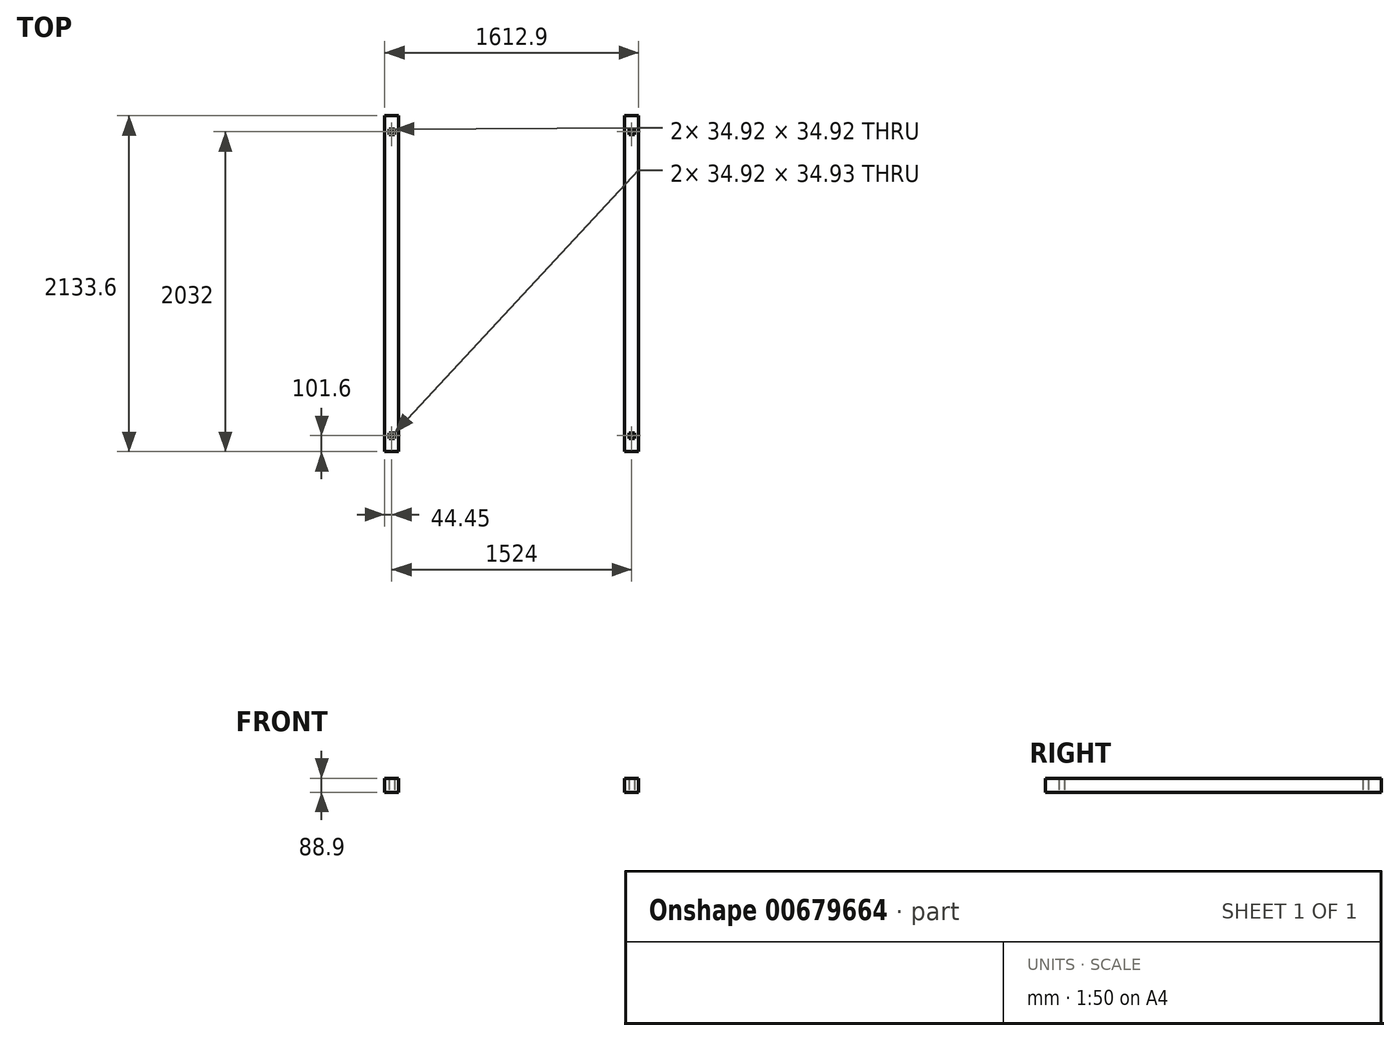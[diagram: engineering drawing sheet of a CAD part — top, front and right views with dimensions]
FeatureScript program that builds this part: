
annotation { "Feature Type Name" : "Feature", "Feature Type Description" : "" }
export const myFeature = defineFeature(function(context is Context, id is Id, definition is map)
    precondition{}
    {
        {
            var Q0;
            Q0=qCreatedBy(makeId("Front.planeOp"),FACE);
            var sketch = newSketch(context, id + "F0", { "sketchPlane" : qUnion([Q0])});
            skLineSegment(sketch, "E0.bottom", {"start": v(0, 0) * mm, "end": v(88.9, 0) * mm});
            skLineSegment(sketch, "E0.top", {"start": v(0, 88.9) * mm, "end": v(88.9, 88.9) * mm});
            skLineSegment(sketch, "E0.left", {"start": v(0, 0) * mm, "end": v(0, 88.9) * mm});
            skLineSegment(sketch, "E0.right", {"start": v(88.9, 0) * mm, "end": v(88.9, 88.9) * mm});
            skSolve(sketch);
        }
        {
            var Q0;
            Q0=makeQuery(id+"F0.imprint","IMPRINT",FACE,{"disambiguationData":[TD([[makeQuery(id+"F0.imprint","IMPRINT",EDGE,{"derivedFrom":sQuery(id+"F0.wireOp",EDGE,"E0.bottom")}),1.0]])]});
            extrude(context, id + "F1", {"entities" : qUnion([Q0]), "depth" : 2133.6 * mm, "offsetDistance" : 25.4 * mm});
        }
        {
            var Q0;
            Q0=makeQuery(id+"F1.opExtrude","SWEPT_FACE",FACE,{"disambiguationData":[OSD([sQuery(id+"F0.wireOp",EDGE,"E0.bottom")])]});
            var sketch = newSketch(context, id + "F2", { "sketchPlane" : qUnion([Q0])});
            skLineSegment(sketch, "E1.bottom", {"start": v(26.99, 119.06) * mm, "end": v(61.91, 119.06) * mm});
            skLineSegment(sketch, "E1.top", {"start": v(26.99, 84.14) * mm, "end": v(61.91, 84.14) * mm});
            skLineSegment(sketch, "E1.left", {"start": v(26.99, 119.06) * mm, "end": v(26.99, 84.14) * mm});
            skLineSegment(sketch, "E1.right", {"start": v(61.91, 119.06) * mm, "end": v(61.91, 84.14) * mm});
            skSolve(sketch);
        }
        {
            var Q0;
            Q0=makeQuery(id+"F2.imprint","IMPRINT",FACE,{"disambiguationData":[TD([[makeQuery(id+"F2.imprint","IMPRINT",EDGE,{"derivedFrom":sQuery(id+"F2.wireOp",EDGE,"E1.bottom")}),-1.0]])]});
            extrude(context, id + "F3", {"entities" : qUnion([Q0]), "operationType" : NewBodyOperationType.REMOVE, "oppositeDirection" : true, "depth" : 91.44 * mm, "offsetDistance" : 25.4 * mm});
        }
        {
            var Q0;
            Q0=makeQuery(id+"F1.opExtrude","SWEPT_FACE",FACE,{"disambiguationData":[OSD([sQuery(id+"F0.wireOp",EDGE,"E0.bottom")])]});
            var sketch = newSketch(context, id + "F4", { "sketchPlane" : qUnion([Q0])});
            skLineSegment(sketch, "E2.bottom", {"start": v(26.99, 2049.46) * mm, "end": v(61.91, 2049.46) * mm});
            skLineSegment(sketch, "E2.top", {"start": v(26.99, 2014.54) * mm, "end": v(61.91, 2014.54) * mm});
            skLineSegment(sketch, "E2.left", {"start": v(26.99, 2049.46) * mm, "end": v(26.99, 2014.54) * mm});
            skLineSegment(sketch, "E2.right", {"start": v(61.91, 2049.46) * mm, "end": v(61.91, 2014.54) * mm});
            skSolve(sketch);
        }
        {
            var Q0;
            Q0=makeQuery(id+"F4.imprint","IMPRINT",FACE,{"disambiguationData":[TD([[makeQuery(id+"F4.imprint","IMPRINT",EDGE,{"derivedFrom":sQuery(id+"F4.wireOp",EDGE,"E2.bottom")}),-1.0]])]});
            extrude(context, id + "F5", {"entities" : qUnion([Q0]), "operationType" : NewBodyOperationType.REMOVE, "oppositeDirection" : true, "depth" : 101.6 * mm, "offsetDistance" : 25.4 * mm});
        }
        {
            var Q0;
            Q0=makeQuery(id+"F1.opExtrude","SWEPT_BODY",BODY,{"disambiguationData":[OSD([sQuery(id+"F0.wireOp",EDGE,"E0.bottom"),sQuery(id+"F0.wireOp",EDGE,"E0.top"),sQuery(id+"F0.wireOp",EDGE,"E0.left"),sQuery(id+"F0.wireOp",EDGE,"E0.right")])]});
            transform(context, id + "F6", {"entities" : qUnion([Q0]), "transformType" : TransformType.TRANSLATION_3D, "dx" : 1524 * mm, "dy" : 0 * mm, "dz" : 0 * mm, "makeCopy" : true});
        }
    });
